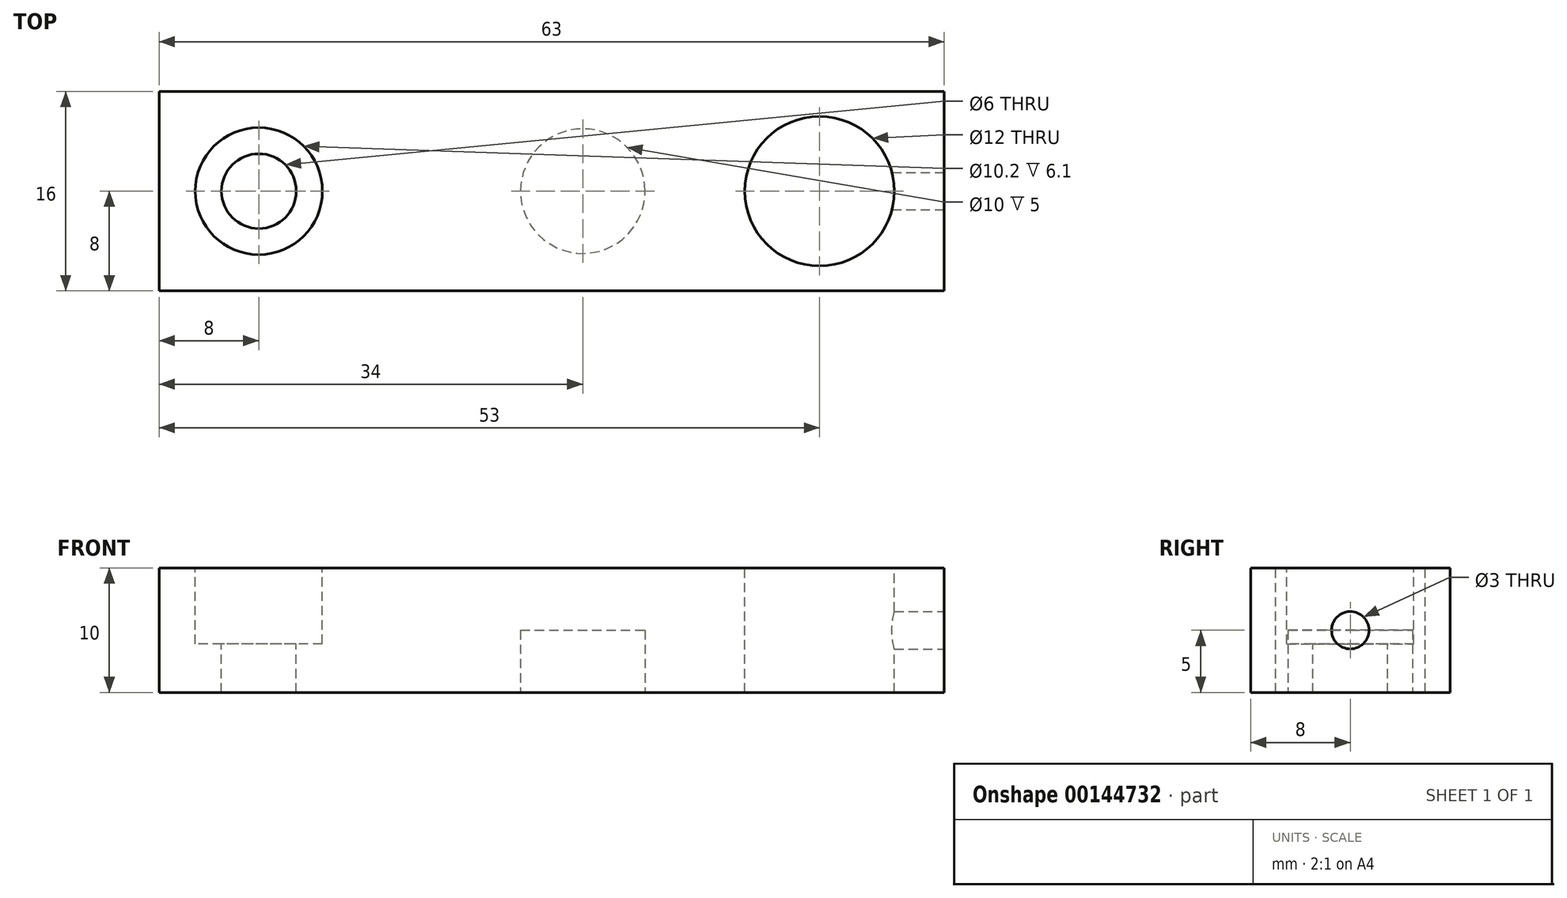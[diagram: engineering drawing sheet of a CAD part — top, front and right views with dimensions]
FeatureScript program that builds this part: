
annotation { "Feature Type Name" : "Feature", "Feature Type Description" : "" }
export const myFeature = defineFeature(function(context is Context, id is Id, definition is map)
    precondition{}
    {
        {
            var Q0;
            Q0=qCreatedBy(makeId("Top.planeOp"),FACE);
            var sketch = newSketch(context, id + "F0", { "sketchPlane" : qUnion([Q0])});
            skLineSegment(sketch, "E0.bottom", {"start": v(0, 0) * mm, "end": v(63, 0) * mm});
            skLineSegment(sketch, "E0.top", {"start": v(0, 16) * mm, "end": v(63, 16) * mm});
            skLineSegment(sketch, "E0.left", {"start": v(0, 0) * mm, "end": v(0, 16) * mm});
            skLineSegment(sketch, "E0.right", {"start": v(63, 0) * mm, "end": v(63, 16) * mm});
            skSolve(sketch);
        }
        {
            var Q0;
            Q0 = qSketchRegion(id + "F0", true);
            extrude(context, id + "F1", {"entities" : qUnion([Q0]), "depth" : 10 * mm});
        }
        {
            var Q0;
            Q0=makeQuery(id+"F1.opExtrude","CAP_FACE",FACE,{"disambiguationData":[OSD([sQuery(id+"F0.wireOp",EDGE,"E0.bottom"),sQuery(id+"F0.wireOp",EDGE,"E0.top"),sQuery(id+"F0.wireOp",EDGE,"E0.left"),sQuery(id+"F0.wireOp",EDGE,"E0.right")])],"isStart":false});
            var sketch = newSketch(context, id + "F2", { "sketchPlane" : qUnion([Q0])});
            skCircle(sketch, "E1", {"center": v(53, 8) * mm, "radius": 6 * mm});
            skCircle(sketch, "E2", {"center": v(8, 8) * mm, "radius": 3 * mm});
            skCircle(sketch, "E3", {"center": v(8, 8) * mm, "radius": 5.1 * mm});
            skSolve(sketch);
        }
        {
            var Q0;
            Q0=makeQuery(id+"F2.imprint","IMPRINT",FACE,{"disambiguationData":[TD([[makeQuery(id+"F2.imprint","IMPRINT",EDGE,{"derivedFrom":sQuery(id+"F2.wireOp",EDGE,"E2")}),1.0]])]});
            var Q1;
            Q1=makeQuery(id+"F2.imprint","IMPRINT",FACE,{"disambiguationData":[TD([[makeQuery(id+"F2.imprint","IMPRINT",EDGE,{"derivedFrom":sQuery(id+"F2.wireOp",EDGE,"E1")}),1.0]])]});
            extrude(context, id + "F3", {"entities" : qUnion([Q0, Q1]), "operationType" : NewBodyOperationType.REMOVE, "endBound" : BoundingType.THROUGH_ALL, "oppositeDirection" : true, "depth" : 25 * mm});
        }
        {
            var Q0;
            Q0=makeQuery(id+"F2.imprint","IMPRINT",FACE,{"disambiguationData":[TD([[makeQuery(id+"F2.imprint","IMPRINT",EDGE,{"derivedFrom":sQuery(id+"F2.wireOp",EDGE,"E2")}),-1.0]])]});
            extrude(context, id + "F4", {"entities" : qUnion([Q0]), "operationType" : NewBodyOperationType.REMOVE, "oppositeDirection" : true, "depth" : 6.1 * mm});
        }
        {
            var Q0;
            Q0=makeQuery(id+"F1.opExtrude","SWEPT_FACE",FACE,{"disambiguationData":[OSD([sQuery(id+"F0.wireOp",EDGE,"E0.right")])]});
            var sketch = newSketch(context, id + "F5", { "sketchPlane" : qUnion([Q0])});
            skCircle(sketch, "E4", {"center": v(8, 5) * mm, "radius": 1.5 * mm});
            skPoint(sketch, "E4.centerSnap0", {"position": v(0, 5) * mm});
            skPoint(sketch, "E4.centerSnap1", {"position": v(8, 10) * mm});
            skSolve(sketch);
        }
        {
            var Q0;
            Q0 = qSketchRegion(id + "F5", true);
            extrude(context, id + "F6", {"entities" : qUnion([Q0]), "operationType" : NewBodyOperationType.REMOVE, "endBound" : BoundingType.UP_TO_NEXT, "oppositeDirection" : true, "depth" : 25 * mm});
        }
        {
            var Q0;
            Q0=makeQuery(id+"F1.opExtrude","CAP_FACE",FACE,{"disambiguationData":[OSD([sQuery(id+"F0.wireOp",EDGE,"E0.bottom"),sQuery(id+"F0.wireOp",EDGE,"E0.top"),sQuery(id+"F0.wireOp",EDGE,"E0.left"),sQuery(id+"F0.wireOp",EDGE,"E0.right")])],"isStart":true});
            var sketch = newSketch(context, id + "F7", { "sketchPlane" : qUnion([Q0])});
            skCircle(sketch, "E5", {"center": v(34, -8) * mm, "radius": 5 * mm});
            skPoint(sketch, "E5.centerSnap0", {"position": v(63, -8) * mm});
            skSolve(sketch);
        }
        {
            var Q0;
            Q0 = qSketchRegion(id + "F7", true);
            extrude(context, id + "F8", {"entities" : qUnion([Q0]), "operationType" : NewBodyOperationType.REMOVE, "oppositeDirection" : true, "depth" : 5 * mm});
        }
    });
